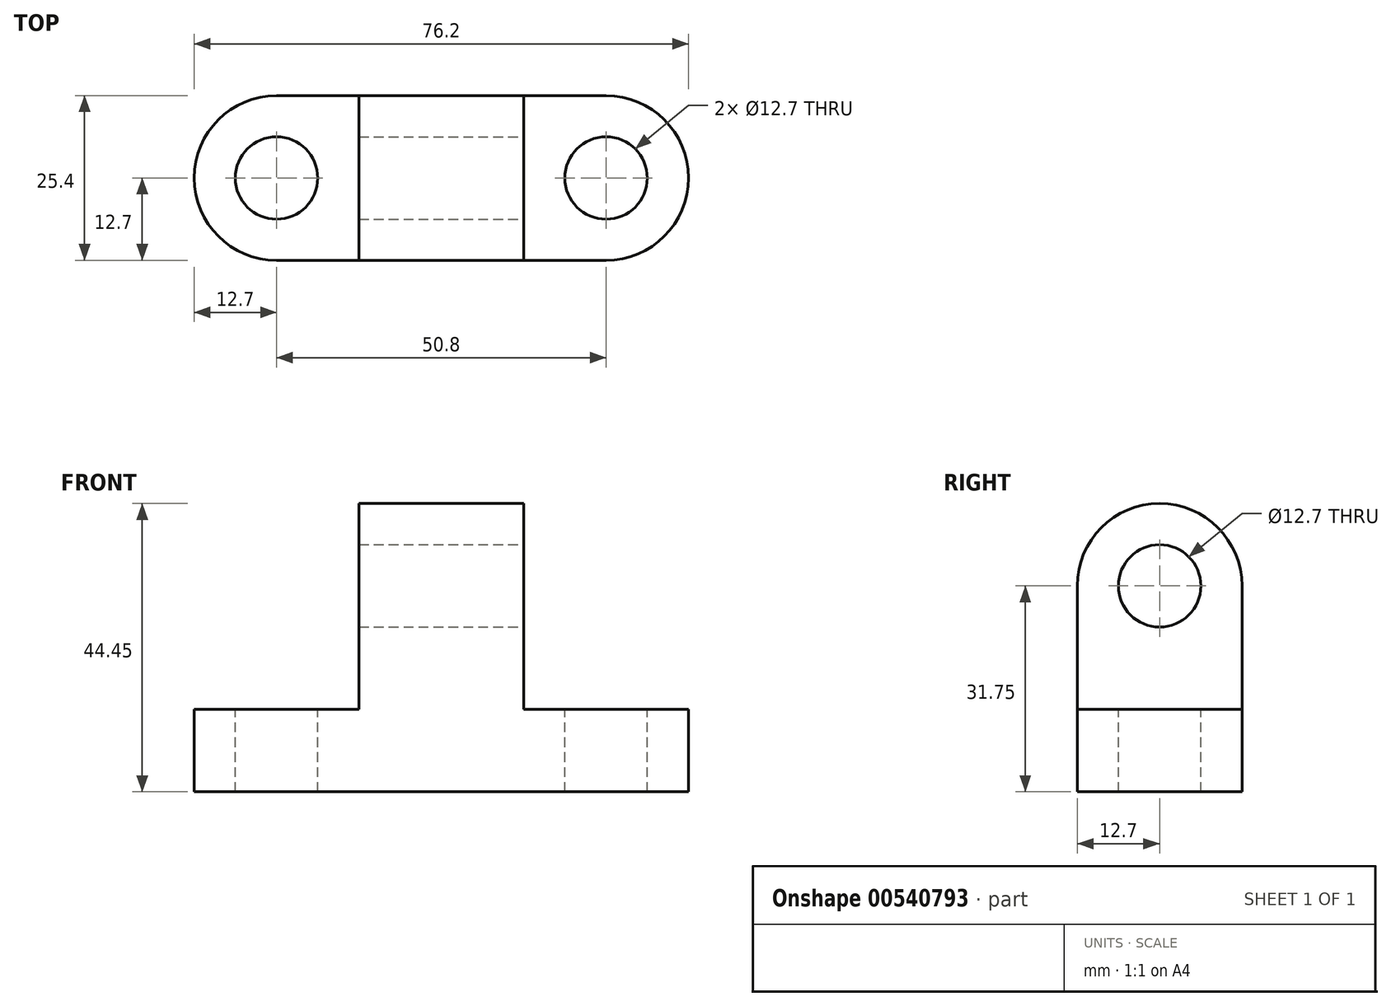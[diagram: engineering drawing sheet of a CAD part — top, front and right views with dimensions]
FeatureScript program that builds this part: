
annotation { "Feature Type Name" : "Feature", "Feature Type Description" : "" }
export const myFeature = defineFeature(function(context is Context, id is Id, definition is map)
    precondition{}
    {
        {
            var Q0;
            Q0=qCreatedBy(makeId("Front.planeOp"),FACE);
            var sketch = newSketch(context, id + "F0", { "sketchPlane" : qUnion([Q0])});
            skLineSegment(sketch, "E0", {"start": v(0, 0) * mm, "end": v(76.2, 0) * mm});
            skLineSegment(sketch, "E1", {"start": v(76.2, 0) * mm, "end": v(76.2, 12.7) * mm});
            skLineSegment(sketch, "E2", {"start": v(76.2, 12.7) * mm, "end": v(50.8, 12.7) * mm});
            skLineSegment(sketch, "E3", {"start": v(50.8, 12.7) * mm, "end": v(50.8, 44.45) * mm});
            skLineSegment(sketch, "E4", {"start": v(50.8, 44.45) * mm, "end": v(25.4, 44.45) * mm});
            skLineSegment(sketch, "E5", {"start": v(25.4, 44.45) * mm, "end": v(25.4, 12.7) * mm});
            skLineSegment(sketch, "E6", {"start": v(25.4, 12.7) * mm, "end": v(0, 12.7) * mm});
            skLineSegment(sketch, "E7", {"start": v(0, 12.7) * mm, "end": v(0, 0) * mm});
            skSolve(sketch);
        }
        {
            var Q0;
            Q0=makeQuery(id+"F0.imprint","IMPRINT",FACE,{"disambiguationData":[TD([[makeQuery(id+"F0.imprint","IMPRINT",EDGE,{"derivedFrom":sQuery(id+"F0.wireOp",EDGE,"E0")}),1.0]])]});
            extrude(context, id + "F1", {"entities" : qUnion([Q0]), "depth" : 25.4 * mm, "offsetDistance" : 25.4 * mm});
        }
        {
            var Q0;
            Q0=makeQuery(id+"F1.opExtrude","SWEPT_FACE",FACE,{"disambiguationData":[OSD([sQuery(id+"F0.wireOp",EDGE,"E3")])]});
            var sketch = newSketch(context, id + "F2", { "sketchPlane" : qUnion([Q0])});
            skCircle(sketch, "E8", {"center": v(-12.7, 31.75) * mm, "radius": 6.35 * mm});
            skArc(sketch, "E9", {"start": v(0, 31.75) * mm, "mid": v(-12.7, 44.45) * mm, "end": v(-25.4, 31.75) * mm});
            skSolve(sketch);
        }
        {
            var Q0;
            Q0=makeQuery(id+"F2.imprint","IMPRINT",FACE,{"disambiguationData":[TD([[makeQuery(id+"F2.imprint","IMPRINT",EDGE,{"derivedFrom":sQuery(id+"F2.wireOp",EDGE,"E8")}),1.0]])]});
            var Q1;
            {var subQ0=sQuery(id+"F2.wireOp",EDGE,"E9");var subQ1=sQuery(id+"F0.wireOp",EDGE,"E3");var subQ2=makeQuery(id+"F1.opExtrude","CAP_EDGE",EDGE,{"disambiguationData":[OSD([subQ1])],"isStart":true});var subQ3=makeQuery(id+"F2.imprint","INTERSECT",VERTEX,{"derivedFrom":[subQ2,subQ0]});Q1=makeQuery(id+"F2.imprint","IMPRINT",FACE,{"disambiguationData":[TD([[makeQuery(id+"F2.imprint","IMPRINT",EDGE,{"disambiguationData":[TD([[subQ3,-1.0]])],"derivedFrom":subQ0}),-1.0]])]});}
            var Q2;
            {var subQ0=sQuery(id+"F2.wireOp",EDGE,"E9");var subQ1=sQuery(id+"F0.wireOp",EDGE,"E3");var subQ2=makeQuery(id+"F1.opExtrude","CAP_EDGE",EDGE,{"disambiguationData":[OSD([subQ1])],"isStart":false});var subQ3=makeQuery(id+"F2.imprint","INTERSECT",VERTEX,{"derivedFrom":[subQ2,subQ0]});Q2=makeQuery(id+"F2.imprint","IMPRINT",FACE,{"disambiguationData":[TD([[makeQuery(id+"F2.imprint","IMPRINT",EDGE,{"disambiguationData":[TD([[subQ3,1.0]])],"derivedFrom":subQ0}),-1.0]])]});}
            extrude(context, id + "F3", {"entities" : qUnion([Q0, Q1, Q2]), "operationType" : NewBodyOperationType.REMOVE, "oppositeDirection" : true, "depth" : 25.4 * mm, "offsetDistance" : 25.4 * mm});
        }
        {
            var Q0;
            Q0=makeQuery(id+"F1.opExtrude","SWEPT_FACE",FACE,{"disambiguationData":[OSD([sQuery(id+"F0.wireOp",EDGE,"E2")])]});
            var sketch = newSketch(context, id + "F4", { "sketchPlane" : qUnion([Q0])});
            skCircle(sketch, "E10", {"center": v(63.5, -12.7) * mm, "radius": 6.35 * mm});
            skCircle(sketch, "E11", {"center": v(12.7, -12.7) * mm, "radius": 6.35 * mm});
            skArc(sketch, "E12", {"start": v(63.5, -25.4) * mm, "mid": v(76.2, -12.7) * mm, "end": v(63.5, 0) * mm});
            skLineSegment(sketch, "E13.0", {"start": v(25.4, -25.4) * mm, "end": v(0, -25.4) * mm});
            skLineSegment(sketch, "E14.0.0", {"start": v(25.4, 0) * mm, "end": v(0, 0) * mm});
            skLineSegment(sketch, "E14.0.1", {"start": v(0, 0) * mm, "end": v(0, -25.4) * mm});
            skLineSegment(sketch, "E14.0.2", {"start": v(0, -25.4) * mm, "end": v(25.4, -25.4) * mm});
            skLineSegment(sketch, "E14.0.3", {"start": v(25.4, -25.4) * mm, "end": v(25.4, 0) * mm});
            skArc(sketch, "E15", {"start": v(12.7, 0) * mm, "mid": v(0, -12.7) * mm, "end": v(12.7, -25.4) * mm});
            skSolve(sketch);
        }
        {
            var Q0;
            {var subQ0=sQuery(id+"F4.wireOp",EDGE,"E14.0.1");var subQ1=sQuery(id+"F4.wireOp",EDGE,"E14.0.0");var subQ2=makeQuery(id+"F4.imprint","INTERSECT",VERTEX,{"derivedFrom":[subQ1,subQ0]});Q0=makeQuery(id+"F4.imprint","IMPRINT",FACE,{"disambiguationData":[TD([[makeQuery(id+"F4.imprint","IMPRINT",EDGE,{"disambiguationData":[TD([[subQ2,1.0]])],"derivedFrom":subQ1}),1.0]])]});}
            var Q1;
            {var subQ0=sQuery(id+"F4.wireOp",EDGE,"E14.0.2");var subQ1=sQuery(id+"F4.wireOp",EDGE,"E14.0.1");var subQ2=makeQuery(id+"F4.imprint","INTERSECT",VERTEX,{"derivedFrom":[subQ1,subQ0]});Q1=makeQuery(id+"F4.imprint","IMPRINT",FACE,{"disambiguationData":[TD([[makeQuery(id+"F4.imprint","IMPRINT",EDGE,{"disambiguationData":[TD([[subQ2,1.0]])],"derivedFrom":subQ1}),1.0]])]});}
            var Q2;
            Q2=makeQuery(id+"F4.imprint","IMPRINT",FACE,{"disambiguationData":[TD([[makeQuery(id+"F4.imprint","IMPRINT",EDGE,{"derivedFrom":sQuery(id+"F4.wireOp",EDGE,"E11")}),1.0]])]});
            var Q3;
            Q3=makeQuery(id+"F4.imprint","IMPRINT",FACE,{"disambiguationData":[TD([[makeQuery(id+"F4.imprint","IMPRINT",EDGE,{"derivedFrom":sQuery(id+"F4.wireOp",EDGE,"E10")}),1.0]])]});
            var Q4;
            {var subQ0=sQuery(id+"F4.wireOp",EDGE,"E12");var subQ1=sQuery(id+"F0.wireOp",EDGE,"E2");var subQ2=makeQuery(id+"F1.opExtrude","CAP_EDGE",EDGE,{"disambiguationData":[OSD([subQ1])],"isStart":true});var subQ3=makeQuery(id+"F4.imprint","INTERSECT",VERTEX,{"derivedFrom":[subQ2,subQ0]});Q4=makeQuery(id+"F4.imprint","IMPRINT",FACE,{"disambiguationData":[TD([[makeQuery(id+"F4.imprint","IMPRINT",EDGE,{"disambiguationData":[TD([[subQ3,1.0]])],"derivedFrom":subQ0}),-1.0]])]});}
            var Q5;
            {var subQ0=sQuery(id+"F4.wireOp",EDGE,"E12");var subQ1=sQuery(id+"F0.wireOp",EDGE,"E2");var subQ2=makeQuery(id+"F1.opExtrude","CAP_EDGE",EDGE,{"disambiguationData":[OSD([subQ1])],"isStart":false});var subQ3=makeQuery(id+"F4.imprint","INTERSECT",VERTEX,{"derivedFrom":[subQ2,subQ0]});Q5=makeQuery(id+"F4.imprint","IMPRINT",FACE,{"disambiguationData":[TD([[makeQuery(id+"F4.imprint","IMPRINT",EDGE,{"disambiguationData":[TD([[subQ3,-1.0]])],"derivedFrom":subQ0}),-1.0]])]});}
            extrude(context, id + "F5", {"entities" : qUnion([Q0, Q1, Q2, Q3, Q4, Q5]), "operationType" : NewBodyOperationType.REMOVE, "oppositeDirection" : true, "depth" : 12.7 * mm, "offsetDistance" : 25.4 * mm});
        }
    });
